# Revit family: LEGRAND_PRISES_VERROUILLEES_ENCASTREES_230_SYMBOLE
name_source: partatom
category: Annotations génériques
revit_build: Autodesk Revit 2018 (Build: 20170223_1515(x64)
units: mm (PartAtom-declared; Revit-internal decimal feet)

## family parameters
Conserve la lisibilité du texte = Non
Partagée = Non
Rotation avec le composant = Non

## types (10) — shared parameters
Prises verrouillées = Oui
diamètre symbole = 10 mm  [stored 0.0328084 ft]
rayon pole = 1 mm  [stored 0.00328084 ft]
rayon symbole = 5 mm  [stored 0.0164042 ft]
rayon verrouillage = 0.8 mm  [stored 0.00262467 ft]

## per-type parameters (varying)
| type | 2P+T | 3P+T | 3P+T+N |
| Symbole réf.052002 | Oui | Non | Non |
| Symbole réf.052012 | Oui | Non | Non |
| Symbole réf.052702 | Oui | Non | Non |
| Symbole réf.053601 | Oui | Non | Non |
| Symbole réf.053812 | Oui | Non | Non |
| Symbole réf.052003 | Non | Oui | Non |
| Symbole réf.052703 | Non | Oui | Non |
| Symbole réf.052713 | Non | Oui | Non |
| Symbole réf.053602 | Non | Oui | Non |
| Symbole réf.052004 | Non | Non | Oui |

note: [stored X ft] marks values corroborated as IEEE doubles in the binary element streams (Revit-internal decimal feet)
